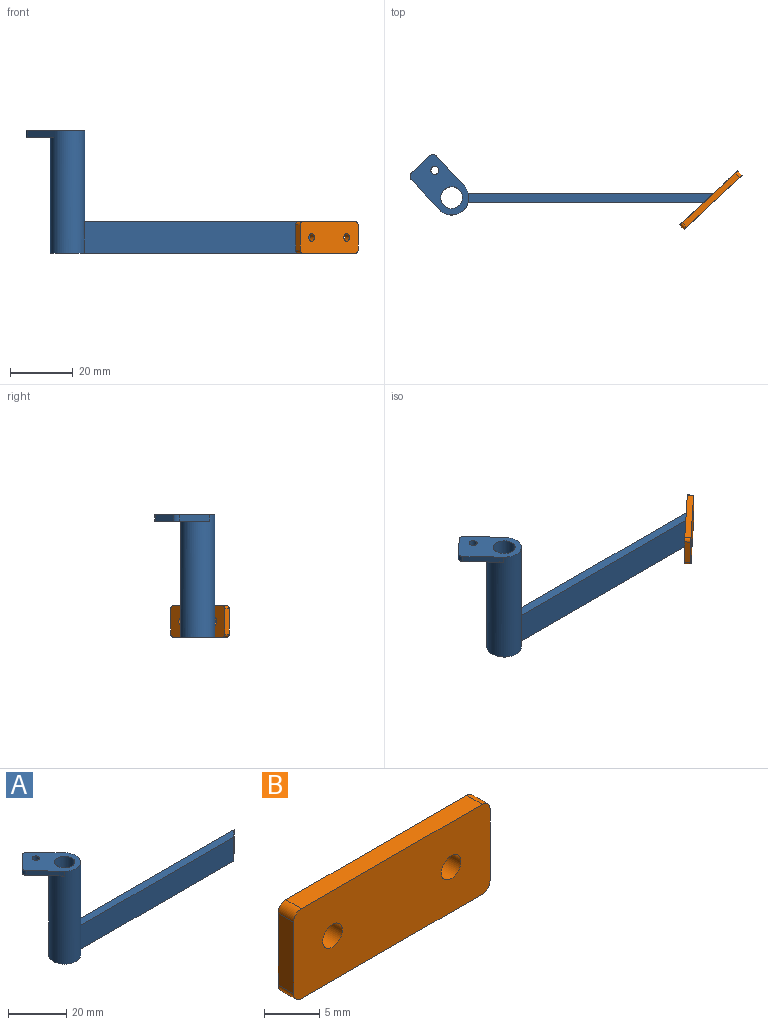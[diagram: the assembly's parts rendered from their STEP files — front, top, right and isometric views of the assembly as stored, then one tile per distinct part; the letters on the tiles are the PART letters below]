
ASSEMBLY  parts=2 mates=1
PART A: 15 faces, bbox 96.9x19.2x39 mm
  f0: plane 89.09x11mm, normal (0,0,-1), area 286.2mm2, adj f1,f2,f3,f4,f6
  f1: cylinder r=5.5mm len=39mm, axis (0,0,-1), area 1282.8mm2, adj f0,f2,f3,f5,f7,f8,f13,f14
  f2: plane 78.3x10mm, normal (0,1,0), area 783mm2, adj f0,f1,f4,f5
  f3: plane 75.08x10mm, normal (0,-1,0), area 750.8mm2, adj f0,f1,f4,f5
  f4: plane 10x3.22mm, normal (0.68,-0.73,0), area 44mm2, adj f0,f2,f3,f5
  f5: plane 78.3x3mm, normal (0,0,1), area 229.7mm2, adj f1,f2,f3,f4
  f6: cylinder r=3.5mm len=39mm, axis (0,0,-1), area 857.7mm2, adj f0,f7
  f7: plane 19.24x18.79mm, normal (0,0,1), area 162.5mm2, adj f1,f6,f8,f9,f10,f11,f12,f13
  f8: plane 9.51x8.87mm, normal (0.73,0.68,0), area 26mm2, adj f1,f7,f9,f14
  f9: cylinder r=1.5mm len=2.12mm, axis (0,0,-1), area 4.7mm2, adj f7,f8,f10,f14
  f10: plane 5.85x5.46mm, normal (-0.68,0.73,0), area 16mm2, adj f7,f9,f11,f14
  f11: cylinder r=1.5mm len=2.12mm, axis (0,0,-1), area 4.7mm2, adj f7,f10,f13,f14
  f12: cylinder r=1.27mm len=2.54mm, axis (0,0,-1), area 16mm2, adj f7,f14
  f13: plane 9.51x8.87mm, normal (-0.73,-0.68,0), area 26mm2, adj f1,f7,f11,f14
  f14: plane 17.49x17.31mm, normal (0,0,-1), area 106mm2, adj f1,f8,f9,f10,f11,f12,f13
PART B: 12 faces, bbox 25.2x2x10 mm
  f0: cylinder r=1mm len=2mm, axis (0,1,0), area 3.1mm2, adj f1,f9,f10,f11
  f1: plane 23.24x2mm, normal (0,0,-1), area 46.5mm2, adj f0,f2,f10,f11
  f2: cylinder r=1mm len=2mm, axis (0,1,0), area 3.1mm2, adj f1,f3,f10,f11
  f3: plane 8x2mm, normal (1,0,0), area 16mm2, adj f2,f4,f10,f11
  f4: cylinder r=1mm len=2mm, axis (0,1,0), area 3.1mm2, adj f3,f5,f10,f11
  f5: plane 23.24x2mm, normal (0,0,1), area 46.5mm2, adj f4,f6,f10,f11
  f6: cylinder r=1mm len=2mm, axis (0,1,0), area 3.1mm2, adj f5,f9,f10,f11
  f7: cylinder r=1.27mm len=2.54mm, axis (0,1,0), area 16mm2, adj f10,f11
  f8: cylinder r=1.27mm len=2.54mm, axis (0,1,0), area 16mm2, adj f10,f11
  f9: plane 8x2mm, normal (-1,0,0), area 16mm2, adj f0,f6,f10,f11
  f10: plane 25.24x10mm, normal (0,-1,0), area 241.4mm2, adj f0,f1,f2,f3,f4,f5,f6,f7
  f11: plane 25.24x10mm, normal (0,1,0), area 241.4mm2, adj f0,f1,f2,f3,f4,f5,f6,f7
PLACE A t=(9.42,-0.01,0)mm
PLACE B rot(axis=(0,0,1),43deg) t=(52.28,5,2.05)mm
MATE fastened B.f11 <-> A.f4  axis (-0.68,0.73,0) through (46.91,-0.01,5)mm
